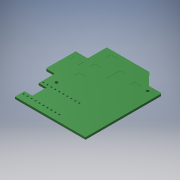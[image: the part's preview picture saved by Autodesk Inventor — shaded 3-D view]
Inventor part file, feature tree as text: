
AUTODESK INVENTOR PART (.ipt)
format: ipt  version: 2018.1 (Build 221171000, 171)  size: 405,504 bytes
history: native  units: mm
features: other x31, extrude x9, sketch x9, reference x5
ambient origin geometry x8: Origin, YZ Plane, XZ Plane, XY Plane, X Axis, Y Axis, Z Axis, Center Point
bodies: Body1 (feature_tree)
feature tree (54):
  other  "ソリッド2"
  other  "ダイレクト編集1"
  other  "ダイレクト編集2"
  other  "ダイレクト編集3"
  extrude  "押し出し1"  Depth=8.8365mm
  other  "ダイレクト編集4"
  other  "ダイレクト編集5"
  extrude  "押し出し2"  Depth=4.0mm
  other  "ダイレクト編集6"
  extrude  "押し出し3"  Depth=10.0mm TaperAngle=0.0deg
  other  "ダイレクト編集7"
  other  "ダイレクト編集8"
  extrude  "押し出し4"  Depth=0.4mm
  extrude  "押し出し5"  Depth=10.0mm TaperAngle=0.0deg
  extrude  "押し出し6"  Depth=10.0mm TaperAngle=0.0deg
  other  "ダイレクト編集9"
  extrude  "押し出し7"  Depth=1.8mm
  extrude  "押し出し8"  Depth=10.0mm TaperAngle=0.0deg
  other  "ダイレクト編集11"
  extrude  "押し出し9"  Depth=3.2mm
  sketch  "スケッチ1"
  reference  "参照1"
  sketch  "スケッチ2"
  sketch  "スケッチ3"
  sketch  "スケッチ4"
  reference  "参照2"
  sketch  "スケッチ5"
  sketch  "スケッチ6"
  sketch  "スケッチ7"
  reference  "参照3"
  sketch  "スケッチ8"
  reference  "参照4"
  sketch  "スケッチ9"
  reference  "参照5"
  other  "ソリッド1"
  other  "尺度1"
  other  "削除1"
  other  "削除2"
  parser-record x2  (decoder bookkeeping rows leaked as tree rows — omitted from the tree; the rows remain in map.json)
  other  "M-R-H.iam"
  other  "R-H-02 v1:1"
  other  "削除3"
  other  "削除4"
  other  "削除5"
  other  "削除6"
  other  "削除7"
  other  "削除8"
  other  "サイズ1"
  other  "削除9"
  other  "削除10"
  other  "Pololu_A_Star_32U4_Micro:1"
  other  "移動2"
  other  "MJ179PH:1"
note: 2 file-system paths scrubbed to <path> (originals preserved in map.json)
